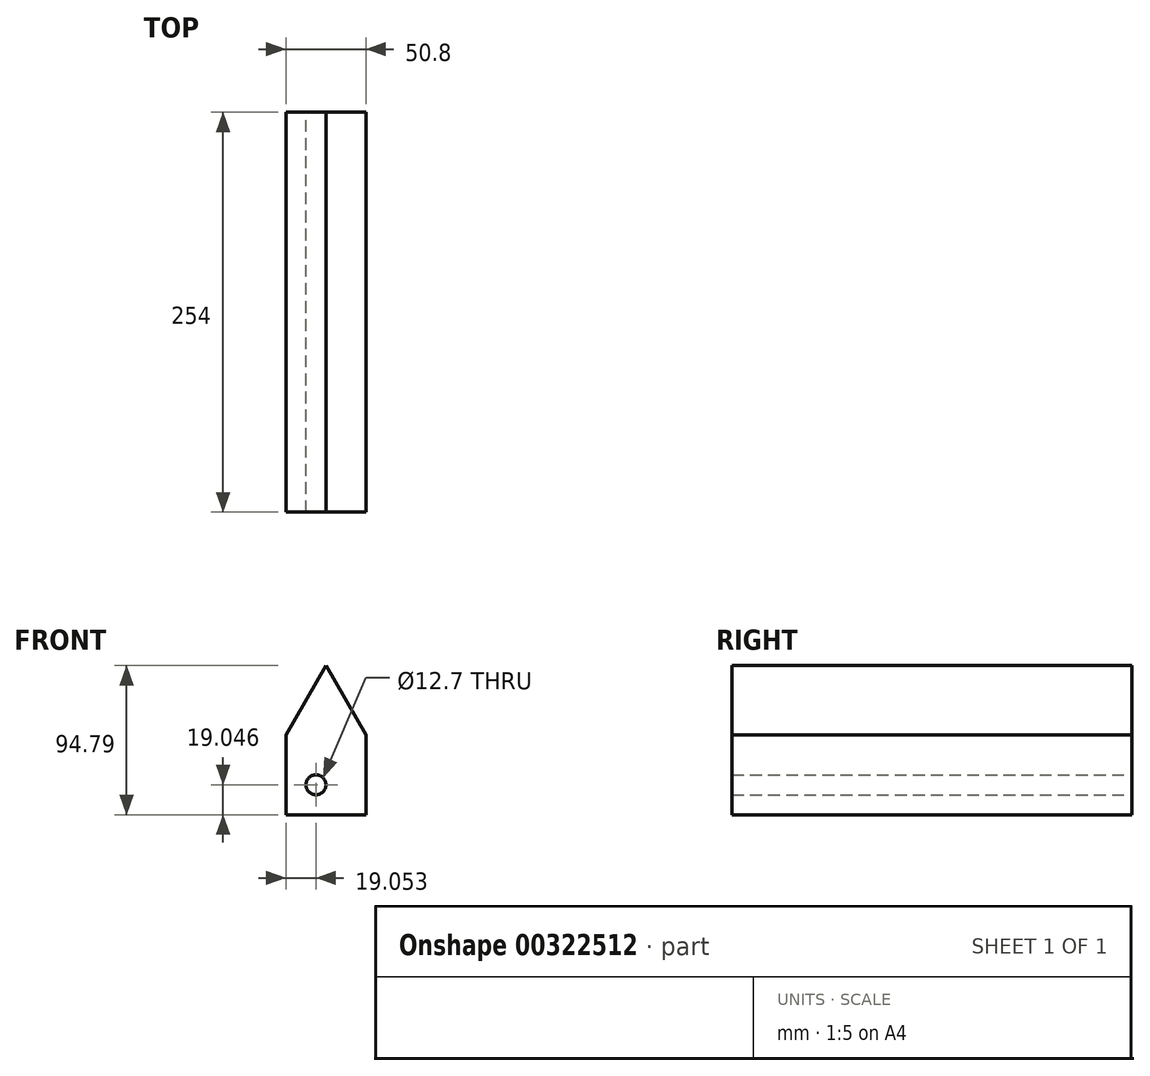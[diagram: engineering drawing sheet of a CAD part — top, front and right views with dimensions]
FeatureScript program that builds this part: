
annotation { "Feature Type Name" : "Feature", "Feature Type Description" : "" }
export const myFeature = defineFeature(function(context is Context, id is Id, definition is map)
    precondition{}
    {
        {
            var Q0;
            Q0=qCreatedBy(makeId("Front.planeOp"),FACE);
            var sketch = newSketch(context, id + "F0", { "sketchPlane" : qUnion([Q0])});
            skLineSegment(sketch, "E0.top", {"start": v(-9.35, -44.04) * mm, "end": v(41.45, -44.04) * mm});
            skLineSegment(sketch, "E0.left", {"start": v(-9.35, 6.76) * mm, "end": v(-9.35, -44.04) * mm});
            skLineSegment(sketch, "E0.right", {"start": v(41.45, 6.76) * mm, "end": v(41.45, -44.04) * mm});
            skLineSegment(sketch, "E1", {"start": v(-9.35, 6.76) * mm, "end": v(16.05, 50.75) * mm});
            skLineSegment(sketch, "E2", {"start": v(16.05, 50.75) * mm, "end": v(41.45, 6.76) * mm});
            skCircle(sketch, "E3", {"center": v(9.7, -25) * mm, "radius": 6.35 * mm});
            skSolve(sketch);
        }
        {
            var Q0;
            Q0=makeQuery(id+"F0.imprint","IMPRINT",FACE,{"disambiguationData":[TD([[makeQuery(id+"F0.imprint","IMPRINT",EDGE,{"derivedFrom":sQuery(id+"F0.wireOp",EDGE,"E0.top")}),1.0]])]});
            extrude(context, id + "F1", {"entities" : qUnion([Q0]), "depth" : 254 * mm});
        }
    });
